# Revit family: Elkay_Drinking-Water_Bottle-Filling-Stations_ezH2O-Liv_Inwall_St1
name_source: partatom
category: Plumbing Fixtures
units: mm (PartAtom-declared; Revit-internal decimal feet)

## family parameters
Always vertical = Yes
Cut with Voids When Loaded = No
Part Type = Normal
Room Calculation Point = No
Round Connector Dimension = Use Diameter
Shared = Yes
Work Plane-Based = No

## types (8) — shared parameters
Activation by = Electronic Bottle Filler Sensor
Installation Location = Indoor
Manufacturer = Elkay
No. of Stations Served = 1
Version = 1.0.0.0

## per-type parameters (varying)
| type | Approx. Shipping Weight | Body_Finish | Bottom pannel | Chilling Capacity | Dimensions (L x W x H) | Finish | Mounting Type | Pannel Finish | Power | Rated Watts | Special Features |
| LBWD00BKC | 40 lbs | Metal - Steel - Stainless - Color 1 | Yes | Non-refrigerated | 5-1/8 inch x 18 inch x 28 inch | Midnight (BK) | Built-in | Black Pannel | 115V/60Hz | 25 | Ambient Water, Automatic Filter Status
Reset, Filtered, Green Ticker™,
Hands Free, Laminar Flow, Visual
Filter Monitor |
| LBWD00WHC | 40 lbs | 304 Stainless Steel | Yes | Non-refrigerated | 5-1/8 inch x 18 inch x 28 inch | Aspen White (WH) | Built-in | Aspen White | 115V/60Hz | 25 | Ambient Water, Automatic Filter Status
Reset, Filtered, Green Ticker™,
Hands Free, Laminar Flow, Visual
Filter Monitor |
| LBWD06BKK | 78 lbs | 304 Stainless Steel | No | 1.5 GPH | 5-1/8 inch x 18 inch x 20-1/2 inch | Midnight (BK) | Built-in | Black Pannel | 115V/60Hz | 165 | Automatic Filter Status Reset, Chilled
Water, Filtered, Green Ticker™,
Hands Free, Laminar Flow, Visual
Filter Monitor |
| LBWD06WHK | 78 lbs | 304 Stainless Steel | No | 1.5 GPH | 5-1/8 inch x 18 inch x 20-1/2 inch | Aspen White (WH) | Built-in | Aspen White | 115V/60Hz | 165 | Automatic Filter Status Reset, Chilled
Water, Filtered, Green Ticker™,
Hands Free, Laminar Flow, Visual
Filter Monitor |
| LBWDC00BKC | 41 lbs | 304 Stainless Steel | Yes | Non-refrigerated | 5-1/8 inch x 18 inch x 28 inch | Midnight (BK) | Wall Mount (Inwall Frame/Plate) | Black Pannel | 115V/60Hz | 25 | Ambient Water, Automatic Filter Status
Reset, Filtered, Green Ticker™,
Hands Free, Laminar Flow, Visual
Filter Monitor |
| LBWDC00WHC | 41 lbs | 304 Stainless Steel | Yes | Non-refrigerated | 5-1/8 inch x 18 inch x 28 inch | Aspen White (WH) | Wall Mount (Inwall Frame/Plate) | Aspen White | 115V/60Hz | 25 | Ambient Water, Automatic Filter Status
Reset, Filtered, Green Ticker™,
Hands Free, Laminar Flow, Visual
Filter Monitor |
| LBWD2C00BKC | 40 lbs | 304 Stainless Steel | No | Non-refrigerated | 5-1/8 inch x 18 inch x 28 inch | Midnight (BK) | Wall Mount (Inwall Frame/Plate) | Black Pannel | 220-240V 50/60Hz | 25 | Ambient Water, Automatic Filter Status
Reset, Filtered, Green Ticker™,
Hands Free, Laminar Flow, Visual
Filter Monitor |
| LBWD2C00WHC | 40 lbs | 304 Stainless Steel | No | Non-refrigerated | 5-1/8 inch x 18 inch x 28 inch | Aspen White (WH) | Wall Mount (Inwall Frame/Plate) | Aspen White | 220-240V 50/60Hz | 25 | Ambient Water, Automatic Filter Status
Reset, Filtered, Green Ticker™,
Hands Free, Laminar Flow, Visual
Filter Monitor |

note: column(s) folded — value = type name in every type: Model

## geometry (parser evidence)
native form markers: Sweep x12
no freeform markers — native parametric forms only
